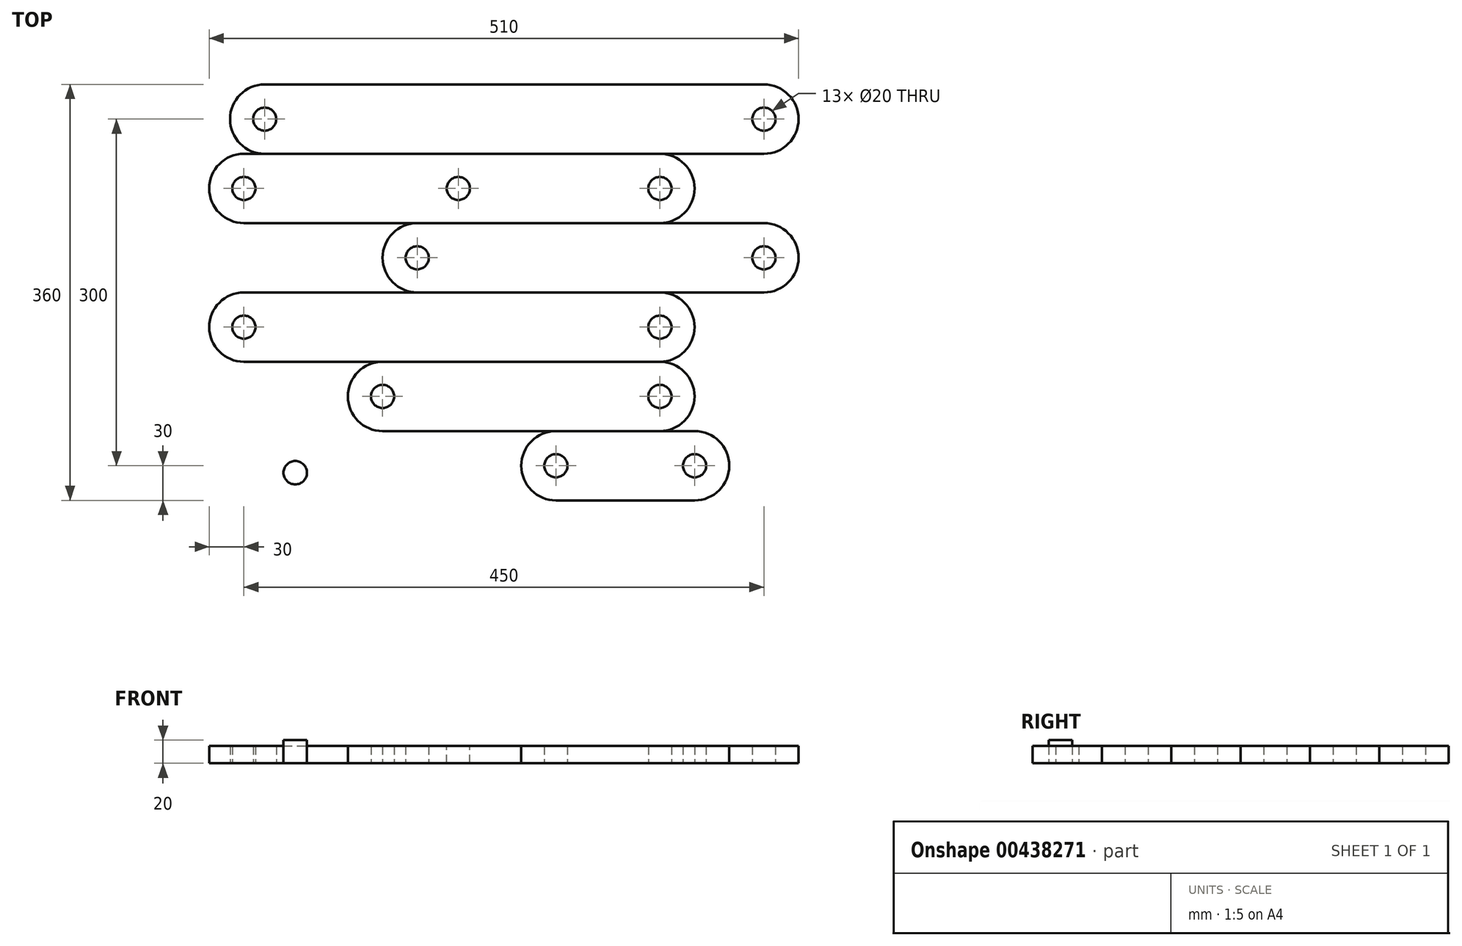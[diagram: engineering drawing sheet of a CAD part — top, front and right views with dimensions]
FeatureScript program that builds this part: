
annotation { "Feature Type Name" : "Feature", "Feature Type Description" : "" }
export const myFeature = defineFeature(function(context is Context, id is Id, definition is map)
    precondition{}
    {
        {
            var Q0;
            Q0=qCreatedBy(makeId("Top.planeOp"),FACE);
            var sketch = newSketch(context, id + "F0", { "sketchPlane" : qUnion([Q0])});
            skCircle(sketch, "E0", {"center": v(0, 0) * mm, "radius": 10 * mm});
            skArc(sketch, "E1", {"start": v(0, 30) * mm, "mid": v(-30, 0) * mm, "end": v(0, -30) * mm});
            skLineSegment(sketch, "E2", {"start": v(0, 30) * mm, "end": v(120, 30) * mm});
            skLineSegment(sketch, "E3", {"start": v(0, -30) * mm, "end": v(120, -30) * mm});
            skArc(sketch, "E4", {"start": v(120, -30) * mm, "mid": v(150, 0) * mm, "end": v(120, 30) * mm});
            skCircle(sketch, "E5", {"center": v(120, 0) * mm, "radius": 10 * mm});
            skSolve(sketch);
        }
        {
            var Q0;
            Q0=makeQuery(id+"F0.imprint","IMPRINT",FACE,{"disambiguationData":[TD([[makeQuery(id+"F0.imprint","IMPRINT",EDGE,{"derivedFrom":sQuery(id+"F0.wireOp",EDGE,"E0")}),-1.0]])]});
            extrude(context, id + "F1", {"entities" : qUnion([Q0]), "depth" : 15 * mm});
        }
        {
            var Q0;
            Q0=qCreatedBy(makeId("Top.planeOp"),FACE);
            var sketch = newSketch(context, id + "F2", { "sketchPlane" : qUnion([Q0])});
            skCircle(sketch, "E6", {"center": v(-150, 0) * mm, "radius": 10 * mm});
            skArc(sketch, "E7", {"start": v(-150, 30) * mm, "mid": v(-180, 0) * mm, "end": v(-150, -30) * mm});
            skLineSegment(sketch, "E8", {"start": v(-150, 30) * mm, "end": v(90, 30) * mm});
            skLineSegment(sketch, "E9", {"start": v(-150, -30) * mm, "end": v(90, -30) * mm});
            skArc(sketch, "E10", {"start": v(90, -30) * mm, "mid": v(120, 0) * mm, "end": v(90, 30) * mm});
            skCircle(sketch, "E11", {"center": v(90, 0) * mm, "radius": 10 * mm});
            skSolve(sketch);
        }
        {
            var Q0;
            Q0=makeQuery(id+"F2.imprint","IMPRINT",FACE,{"disambiguationData":[TD([[makeQuery(id+"F2.imprint","IMPRINT",EDGE,{"derivedFrom":sQuery(id+"F2.wireOp",EDGE,"E6")}),-1.0]])]});
            extrude(context, id + "F3", {"entities" : qUnion([Q0]), "depth" : 15 * mm});
        }
        {
            var Q0;
            Q0=makeQuery(id+"F3.opExtrude","SWEPT_BODY",BODY,{"disambiguationData":[OSD([sQuery(id+"F2.wireOp",EDGE,"E6"),sQuery(id+"F2.wireOp",EDGE,"E7"),sQuery(id+"F2.wireOp",EDGE,"E8"),sQuery(id+"F2.wireOp",EDGE,"E9"),sQuery(id+"F2.wireOp",EDGE,"E10"),sQuery(id+"F2.wireOp",EDGE,"E11")])]});
            transform(context, id + "F4", {"entities" : qUnion([Q0]), "transformType" : TransformType.TRANSLATION_3D, "dx" : 0 * mm, "dy" : 60 * mm, "dz" : 0 * mm, "makeCopy" : false});
        }
        {
            var Q0;
            Q0=qCreatedBy(makeId("Top.planeOp"),FACE);
            var sketch = newSketch(context, id + "F5", { "sketchPlane" : qUnion([Q0])});
            skCircle(sketch, "E12", {"center": v(-270, 0) * mm, "radius": 10 * mm});
            skArc(sketch, "E13", {"start": v(-270, 30) * mm, "mid": v(-300, 0) * mm, "end": v(-270, -30) * mm});
            skLineSegment(sketch, "E14", {"start": v(-270, 30) * mm, "end": v(90, 30) * mm});
            skLineSegment(sketch, "E15", {"start": v(-270, -30) * mm, "end": v(90, -30) * mm});
            skArc(sketch, "E16", {"start": v(90, -30) * mm, "mid": v(120, 0) * mm, "end": v(90, 30) * mm});
            skCircle(sketch, "E17", {"center": v(90, 0) * mm, "radius": 10 * mm});
            skSolve(sketch);
        }
        {
            var Q0;
            Q0=makeQuery(id+"F5.imprint","IMPRINT",FACE,{"disambiguationData":[TD([[makeQuery(id+"F5.imprint","IMPRINT",EDGE,{"derivedFrom":sQuery(id+"F5.wireOp",EDGE,"E12")}),-1.0]])]});
            extrude(context, id + "F6", {"entities" : qUnion([Q0]), "depth" : 15 * mm});
        }
        {
            var Q0;
            Q0=makeQuery(id+"F6.opExtrude","SWEPT_BODY",BODY,{"disambiguationData":[OSD([sQuery(id+"F5.wireOp",EDGE,"E12"),sQuery(id+"F5.wireOp",EDGE,"E13"),sQuery(id+"F5.wireOp",EDGE,"E14"),sQuery(id+"F5.wireOp",EDGE,"E15"),sQuery(id+"F5.wireOp",EDGE,"E16"),sQuery(id+"F5.wireOp",EDGE,"E17")])]});
            transform(context, id + "F7", {"entities" : qUnion([Q0]), "transformType" : TransformType.TRANSLATION_3D, "dx" : 0 * mm, "dy" : 120 * mm, "dz" : 0 * mm, "makeCopy" : false});
        }
        {
            var Q0;
            Q0=qCreatedBy(makeId("Top.planeOp"),FACE);
            var sketch = newSketch(context, id + "F8", { "sketchPlane" : qUnion([Q0])});
            skCircle(sketch, "E18", {"center": v(-120, 0) * mm, "radius": 10 * mm});
            skArc(sketch, "E19", {"start": v(-120, 30) * mm, "mid": v(-150, 0) * mm, "end": v(-120, -30) * mm});
            skLineSegment(sketch, "E20", {"start": v(-120, 30) * mm, "end": v(180, 30) * mm});
            skLineSegment(sketch, "E21", {"start": v(-120, -30) * mm, "end": v(180, -30) * mm});
            skArc(sketch, "E22", {"start": v(180, -30) * mm, "mid": v(210, 0) * mm, "end": v(180, 30) * mm});
            skCircle(sketch, "E23", {"center": v(180, 0) * mm, "radius": 10 * mm});
            skSolve(sketch);
        }
        {
            var Q0;
            Q0=makeQuery(id+"F8.imprint","IMPRINT",FACE,{"disambiguationData":[TD([[makeQuery(id+"F8.imprint","IMPRINT",EDGE,{"derivedFrom":sQuery(id+"F8.wireOp",EDGE,"E18")}),-1.0]])]});
            extrude(context, id + "F9", {"entities" : qUnion([Q0]), "depth" : 15 * mm});
        }
        {
            var Q0;
            Q0=makeQuery(id+"F9.opExtrude","SWEPT_BODY",BODY,{"disambiguationData":[OSD([sQuery(id+"F8.wireOp",EDGE,"E18"),sQuery(id+"F8.wireOp",EDGE,"E19"),sQuery(id+"F8.wireOp",EDGE,"E20"),sQuery(id+"F8.wireOp",EDGE,"E21"),sQuery(id+"F8.wireOp",EDGE,"E22"),sQuery(id+"F8.wireOp",EDGE,"E23")])]});
            transform(context, id + "F10", {"entities" : qUnion([Q0]), "transformType" : TransformType.TRANSLATION_3D, "dx" : 0 * mm, "dy" : 180 * mm, "dz" : 0 * mm, "makeCopy" : false});
        }
        {
            var Q0;
            Q0=qCreatedBy(makeId("Top.planeOp"),FACE);
            var sketch = newSketch(context, id + "F11", { "sketchPlane" : qUnion([Q0])});
            skCircle(sketch, "E24", {"center": v(-225.6, -5.99) * mm, "radius": 10.14 * mm});
            skSolve(sketch);
        }
        {
            var Q0;
            Q0=makeQuery(id+"F11.imprint","IMPRINT",FACE,{"disambiguationData":[TD([[makeQuery(id+"F11.imprint","IMPRINT",EDGE,{"derivedFrom":sQuery(id+"F11.wireOp",EDGE,"E24")}),1.0]])]});
            extrude(context, id + "F12", {"entities" : qUnion([Q0]), "depth" : 20 * mm});
        }
        {
            var Q0;
            Q0=makeQuery(id+"F6.opExtrude","SWEPT_BODY",BODY,{"disambiguationData":[OSD([sQuery(id+"F5.wireOp",EDGE,"E12"),sQuery(id+"F5.wireOp",EDGE,"E13"),sQuery(id+"F5.wireOp",EDGE,"E14"),sQuery(id+"F5.wireOp",EDGE,"E15"),sQuery(id+"F5.wireOp",EDGE,"E16"),sQuery(id+"F5.wireOp",EDGE,"E17")])]});
            transform(context, id + "F13", {"entities" : qUnion([Q0]), "transformType" : TransformType.TRANSLATION_3D, "dx" : 0 * mm, "dy" : 120 * mm, "dz" : 0 * mm, "makeCopy" : true});
        }
        {
            var Q0;
            Q0=makeQuery(id+"F13.opPattern","COPY",FACE,{"derivedFrom":makeQuery(id+"F6.opExtrude","CAP_FACE",FACE,{"disambiguationData":[OSD([sQuery(id+"F5.wireOp",EDGE,"E12"),sQuery(id+"F5.wireOp",EDGE,"E13"),sQuery(id+"F5.wireOp",EDGE,"E14"),sQuery(id+"F5.wireOp",EDGE,"E15"),sQuery(id+"F5.wireOp",EDGE,"E16"),sQuery(id+"F5.wireOp",EDGE,"E17")])],"isStart":false}),"instanceName":"1"});
            var sketch = newSketch(context, id + "F14", { "sketchPlane" : qUnion([Q0])});
            skCircle(sketch, "E25", {"center": v(-84.43, 240) * mm, "radius": 10 * mm});
            skSolve(sketch);
        }
        {
            var Q0;
            Q0=makeQuery(id+"F14.imprint","IMPRINT",FACE,{"disambiguationData":[TD([[makeQuery(id+"F14.imprint","IMPRINT",EDGE,{"derivedFrom":sQuery(id+"F14.wireOp",EDGE,"E25")}),1.0]])]});
            extrude(context, id + "F15", {"entities" : qUnion([Q0]), "operationType" : NewBodyOperationType.REMOVE, "endBound" : BoundingType.THROUGH_ALL, "oppositeDirection" : true, "depth" : 25 * mm});
        }
        {
            var Q0;
            Q0=qCreatedBy(makeId("Top.planeOp"),FACE);
            var sketch = newSketch(context, id + "F16", { "sketchPlane" : qUnion([Q0])});
            skCircle(sketch, "E26", {"center": v(-252, 0) * mm, "radius": 10 * mm});
            skArc(sketch, "E27", {"start": v(-252, 30) * mm, "mid": v(-282, 0) * mm, "end": v(-252, -30) * mm});
            skLineSegment(sketch, "E28", {"start": v(-252, 30) * mm, "end": v(180, 30) * mm});
            skLineSegment(sketch, "E29", {"start": v(-252, -30) * mm, "end": v(180, -30) * mm});
            skArc(sketch, "E30", {"start": v(180, -30) * mm, "mid": v(210, 0) * mm, "end": v(180, 30) * mm});
            skCircle(sketch, "E31", {"center": v(180, 0) * mm, "radius": 10 * mm});
            skSolve(sketch);
        }
        {
            var Q0;
            Q0=qSketchRegion(id+"F16",true);
            extrude(context, id + "F17", {"entities" : qUnion([Q0]), "depth" : 15 * mm});
        }
        {
            var Q0;
            Q0=makeQuery(id+"F17.opExtrude","SWEPT_BODY",BODY,{"disambiguationData":[OSD([sQuery(id+"F16.wireOp",EDGE,"E26"),sQuery(id+"F16.wireOp",EDGE,"E27"),sQuery(id+"F16.wireOp",EDGE,"E28"),sQuery(id+"F16.wireOp",EDGE,"E29"),sQuery(id+"F16.wireOp",EDGE,"E30"),sQuery(id+"F16.wireOp",EDGE,"E31")])]});
            transform(context, id + "F18", {"entities" : qUnion([Q0]), "transformType" : TransformType.TRANSLATION_3D, "dx" : 0 * mm, "dy" : 300 * mm, "dz" : 0 * mm, "makeCopy" : false});
        }
    });
